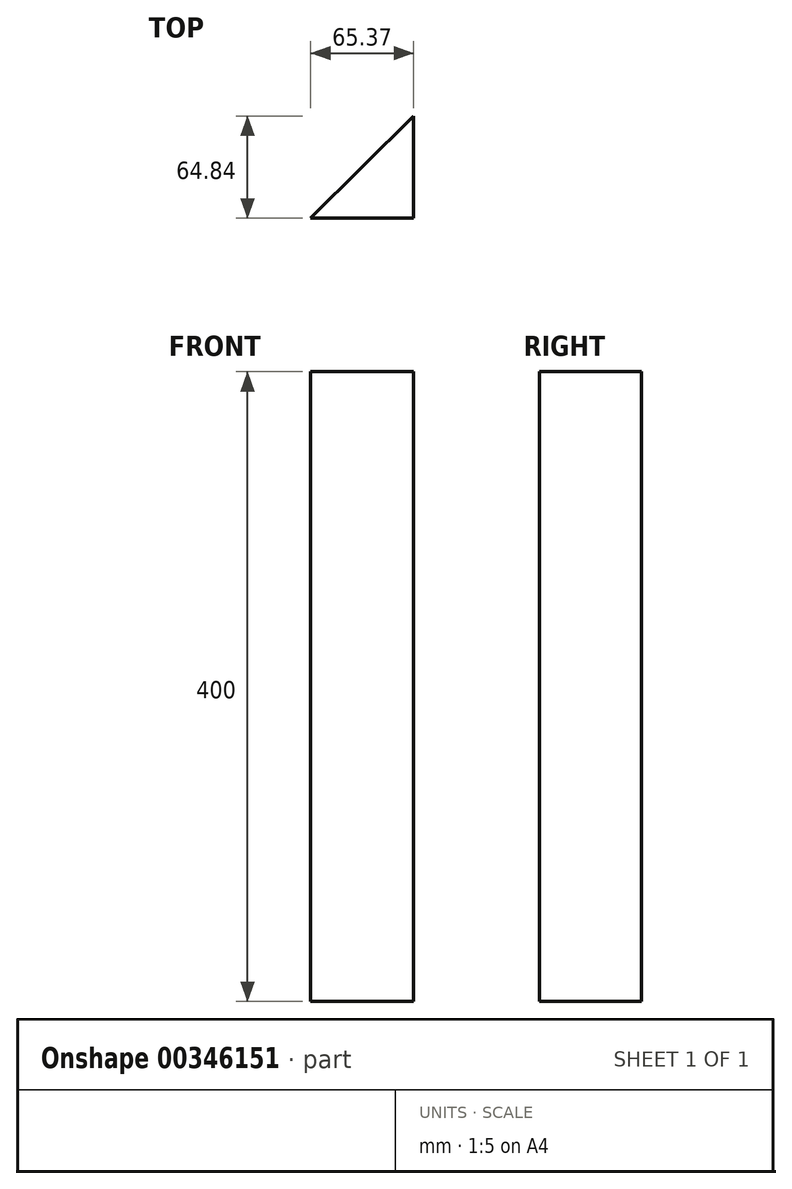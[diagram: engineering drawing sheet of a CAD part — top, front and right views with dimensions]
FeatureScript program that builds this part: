
annotation { "Feature Type Name" : "Feature", "Feature Type Description" : "" }
export const myFeature = defineFeature(function(context is Context, id is Id, definition is map)
    precondition{}
    {
        {
            var Q0;
            Q0=qCreatedBy(makeId("Top.planeOp"),FACE);
            var sketch = newSketch(context, id + "F0", { "sketchPlane" : qUnion([Q0])});
            skLineSegment(sketch, "E0", {"start": v(-38.6, -30.65) * mm, "end": v(26.77, -30.65) * mm});
            skLineSegment(sketch, "E1", {"start": v(26.77, -30.65) * mm, "end": v(26.77, 34.19) * mm});
            skLineSegment(sketch, "E2", {"start": v(26.77, 34.19) * mm, "end": v(-38.6, -30.65) * mm});
            skSolve(sketch);
        }
        {
            var Q0;
            Q0=makeQuery(id+"F0.imprint","IMPRINT",FACE,{"disambiguationData":[TD([[makeQuery(id+"F0.imprint","IMPRINT",EDGE,{"derivedFrom":sQuery(id+"F0.wireOp",EDGE,"E0")}),1.0]])]});
            var sketch = newSketch(context, id + "F1", { "sketchPlane" : qUnion([Q0])});
            skSolve(sketch);
        }
        {
            var Q0;
            Q0 = qSketchRegion(id + "F1", true);
            var Q1;
            Q1=makeQuery(id+"F1.imprint","IMPRINT",FACE,{"disambiguationData":[TD([[makeQuery(id+"F1.imprint","IMPRINT",EDGE,{"derivedFrom":makeQuery(id+"F0.imprint","IMPRINT",EDGE,{"derivedFrom":sQuery(id+"F0.wireOp",EDGE,"E0")})}),1.0]])]});
            var Q2;
            Q2=makeQuery(id+"F0.imprint","IMPRINT",FACE,{"disambiguationData":[TD([[makeQuery(id+"F0.imprint","IMPRINT",EDGE,{"derivedFrom":sQuery(id+"F0.wireOp",EDGE,"E0")}),1.0]])]});
            extrude(context, id + "F2", {"entities" : qUnion([Q0, Q1, Q2]), "depth" : 400 * mm});
        }
    });
